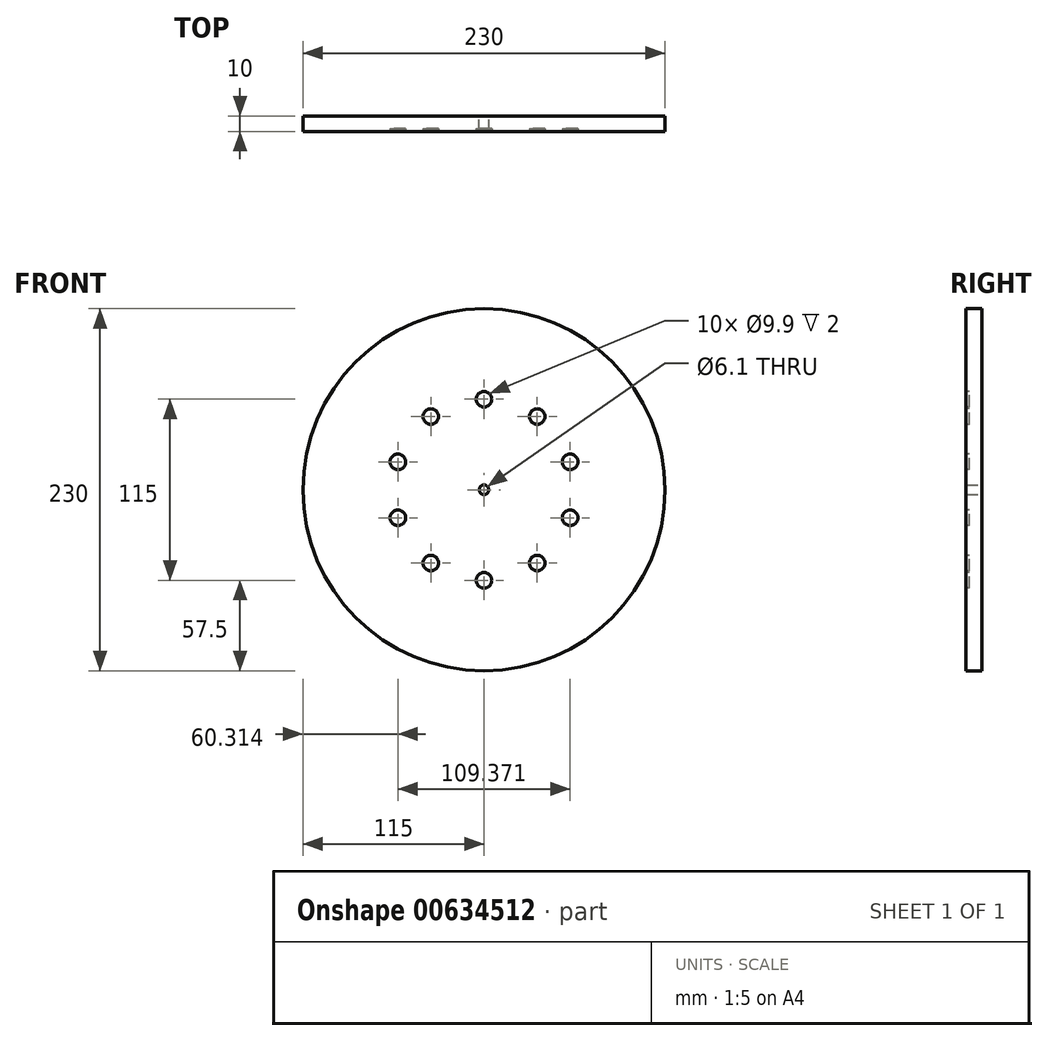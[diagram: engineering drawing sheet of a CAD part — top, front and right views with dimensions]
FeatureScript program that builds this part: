
annotation { "Feature Type Name" : "Feature", "Feature Type Description" : "" }
export const myFeature = defineFeature(function(context is Context, id is Id, definition is map)
    precondition{}
    {
        {
            var Q0;
            Q0=qCreatedBy(makeId("Front.planeOp"),FACE);
            var sketch = newSketch(context, id + "F0", { "sketchPlane" : qUnion([Q0])});
            skCircle(sketch, "E0", {"center": v(0, 0) * mm, "radius": 115 * mm});
            skCircle(sketch, "E1", {"center": v(0, 0) * mm, "radius": 3.05 * mm});
            skSolve(sketch);
        }
        {
            var Q0;
            Q0 = qSketchRegion(id + "F0", true);
            extrude(context, id + "F1", {"entities" : qUnion([Q0]), "depth" : 10 * mm, "offsetDistance" : 25 * mm});
        }
        {
            var Q0;
            Q0=makeQuery(id+"F1.opExtrude","CAP_FACE",FACE,{"disambiguationData":[OSD([sQuery(id+"F0.wireOp",EDGE,"E0"),sQuery(id+"F0.wireOp",EDGE,"E1")])],"isStart":false});
            var sketch = newSketch(context, id + "F2", { "sketchPlane" : qUnion([Q0])});
            skCircle(sketch, "E2", {"center": v(0, 57.5) * mm, "radius": 4.95 * mm});
            skCircle(sketch, "E3.1.0", {"center": v(-33.8, 46.52) * mm, "radius": 4.95 * mm});
            skCircle(sketch, "E3.2.0", {"center": v(-54.69, 17.77) * mm, "radius": 4.95 * mm});
            skCircle(sketch, "E3.3.0", {"center": v(-54.69, -17.77) * mm, "radius": 4.95 * mm});
            skCircle(sketch, "E3.4.0", {"center": v(-33.8, -46.52) * mm, "radius": 4.95 * mm});
            skCircle(sketch, "E3.5.0", {"center": v(0, -57.5) * mm, "radius": 4.95 * mm});
            skCircle(sketch, "E3.6.0", {"center": v(33.8, -46.52) * mm, "radius": 4.95 * mm});
            skCircle(sketch, "E3.7.0", {"center": v(54.69, -17.77) * mm, "radius": 4.95 * mm});
            skCircle(sketch, "E3.8.0", {"center": v(54.69, 17.77) * mm, "radius": 4.95 * mm});
            skCircle(sketch, "E3.9.0", {"center": v(33.8, 46.52) * mm, "radius": 4.95 * mm});
            skPoint(sketch, "E3.center", {"position": v(0, 0) * mm});
            skSolve(sketch);
        }
        {
            var Q0;
            Q0 = qSketchRegion(id + "F2", true);
            extrude(context, id + "F3", {"entities" : qUnion([Q0]), "operationType" : NewBodyOperationType.REMOVE, "oppositeDirection" : true, "depth" : 2 * mm, "offsetDistance" : 25 * mm});
        }
    });
